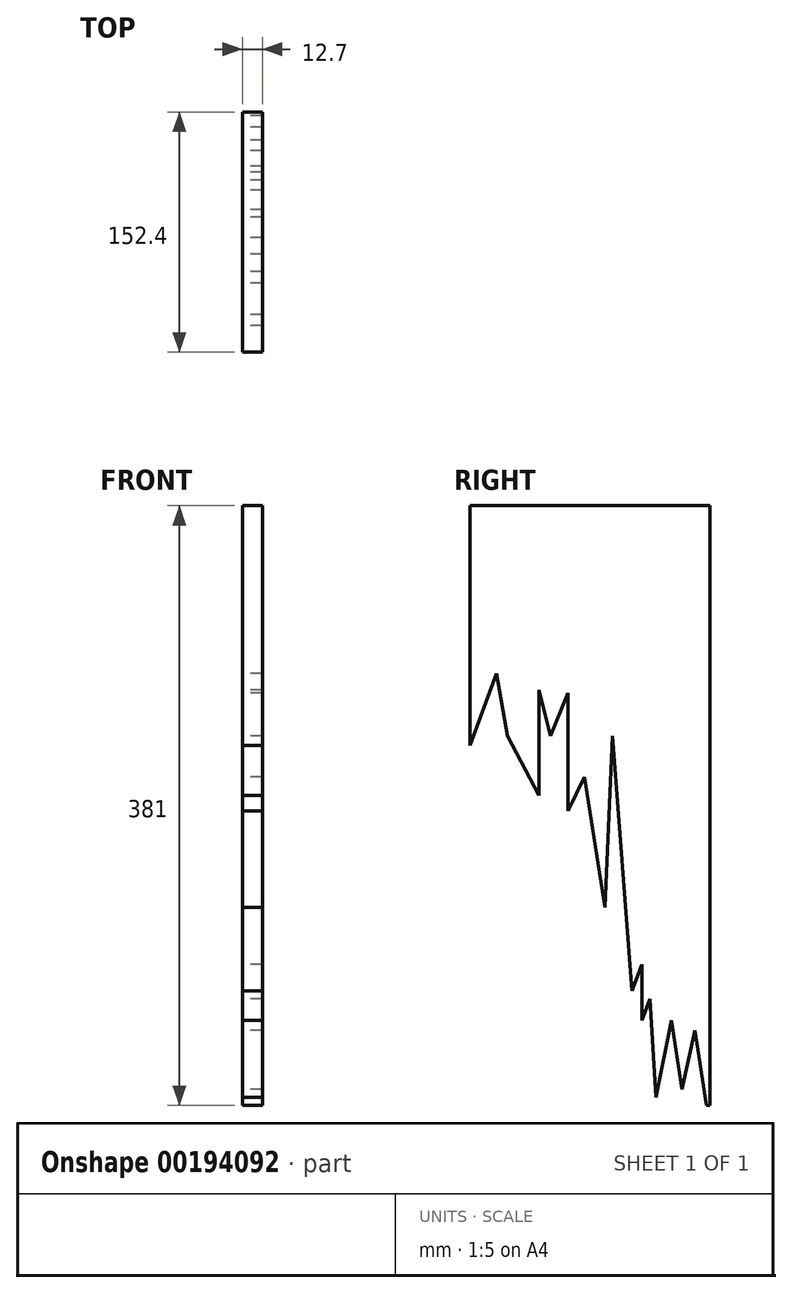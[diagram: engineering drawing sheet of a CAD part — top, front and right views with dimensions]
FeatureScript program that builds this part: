
annotation { "Feature Type Name" : "Feature", "Feature Type Description" : "" }
export const myFeature = defineFeature(function(context is Context, id is Id, definition is map)
    precondition{}
    {
        {
            var Q0;
            Q0=qCreatedBy(makeId("Right.planeOp"),FACE);
            var sketch = newSketch(context, id + "F0", { "sketchPlane" : qUnion([Q0])});
            skLineSegment(sketch, "E0", {"start": v(-81.15, 0) * mm, "end": v(-81.15, 152.4) * mm});
            skLineSegment(sketch, "E1", {"start": v(-81.15, 152.4) * mm, "end": v(71.25, 152.4) * mm});
            skLineSegment(sketch, "E2", {"start": v(71.25, 152.4) * mm, "end": v(71.25, -228.6) * mm});
            skLineSegment(sketch, "E3", {"start": v(-81.15, 0) * mm, "end": v(-64.26, 45.8) * mm});
            skLineSegment(sketch, "E4", {"start": v(-64.26, 45.8) * mm, "end": v(-57.4, 6.1) * mm});
            skLineSegment(sketch, "E5", {"start": v(-57.4, 6.1) * mm, "end": v(-37.22, -31.82) * mm});
            skLineSegment(sketch, "E6", {"start": v(-37.22, -31.82) * mm, "end": v(-37.22, 35.31) * mm});
            skLineSegment(sketch, "E7", {"start": v(-37.22, 35.31) * mm, "end": v(-30.09, 6.1) * mm});
            skLineSegment(sketch, "E8", {"start": v(-30.09, 6.1) * mm, "end": v(-19.02, 33.25) * mm});
            skLineSegment(sketch, "E9", {"start": v(-19.02, 33.25) * mm, "end": v(-19.02, -41.58) * mm});
            skLineSegment(sketch, "E10", {"start": v(-19.02, -41.58) * mm, "end": v(-8.5, -19.86) * mm});
            skLineSegment(sketch, "E11", {"start": v(-8.5, -19.86) * mm, "end": v(4.48, -102.95) * mm});
            skLineSegment(sketch, "E12", {"start": v(4.48, -102.95) * mm, "end": v(9.24, 6.1) * mm});
            skLineSegment(sketch, "E13", {"start": v(9.24, 6.1) * mm, "end": v(21.87, -155.96) * mm});
            skLineSegment(sketch, "E14", {"start": v(21.87, -155.96) * mm, "end": v(28.11, -139.02) * mm});
            skLineSegment(sketch, "E15", {"start": v(28.11, -139.02) * mm, "end": v(28.11, -174.6) * mm});
            skLineSegment(sketch, "E16", {"start": v(28.11, -174.6) * mm, "end": v(33.1, -161.07) * mm});
            skLineSegment(sketch, "E17", {"start": v(33.1, -161.07) * mm, "end": v(37.13, -223.37) * mm});
            skLineSegment(sketch, "E18", {"start": v(37.13, -223.37) * mm, "end": v(46.75, -174.6) * mm});
            skLineSegment(sketch, "E19", {"start": v(46.75, -174.6) * mm, "end": v(53.57, -218.25) * mm});
            skLineSegment(sketch, "E20", {"start": v(53.57, -218.25) * mm, "end": v(61.62, -180.89) * mm});
            skLineSegment(sketch, "E21", {"start": v(61.62, -180.89) * mm, "end": v(69.07, -228.6) * mm});
            skLineSegment(sketch, "E22", {"start": v(69.07, -228.6) * mm, "end": v(71.25, -228.6) * mm});
            skSolve(sketch);
        }
        {
            var Q0;
            Q0 = qSketchRegion(id + "F0", true);
            extrude(context, id + "F1", {"entities" : qUnion([Q0]), "depth" : 12.7 * mm});
        }
    });
